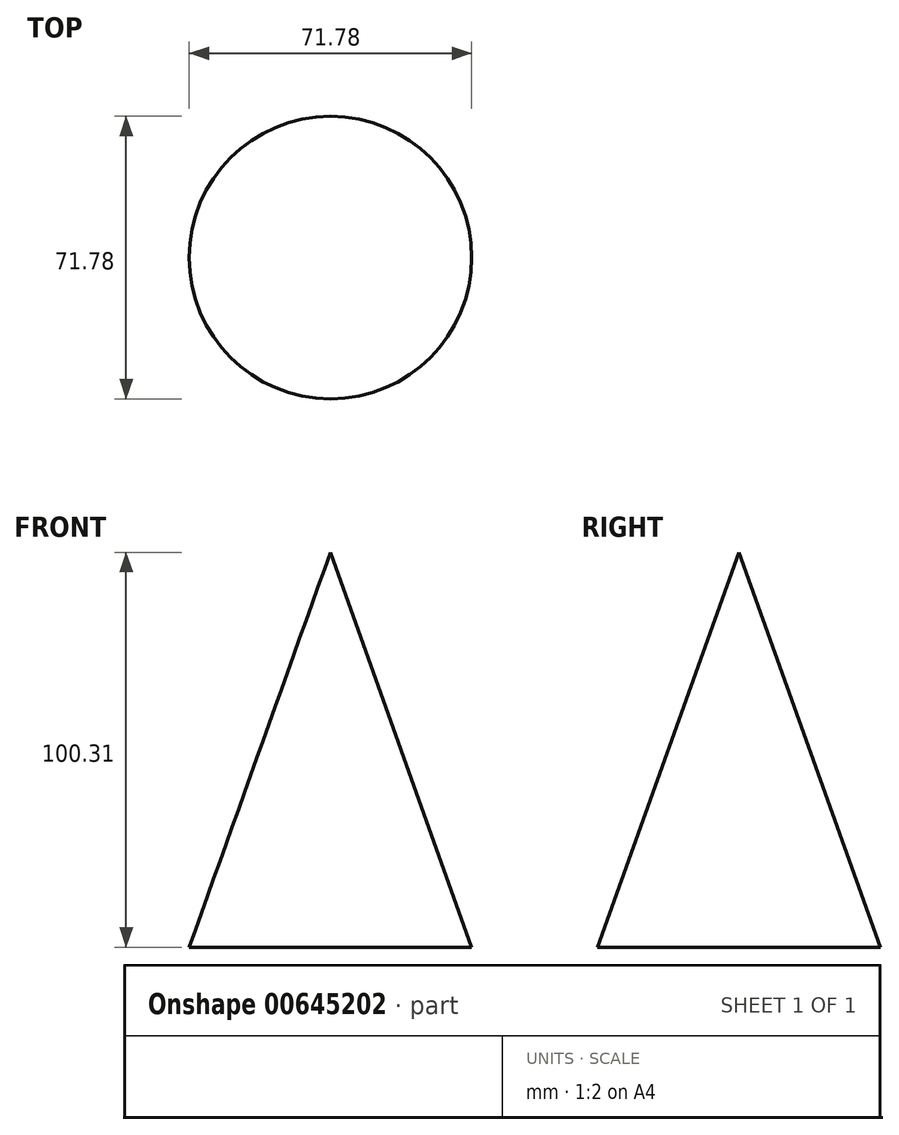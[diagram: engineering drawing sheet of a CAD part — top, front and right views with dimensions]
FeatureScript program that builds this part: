
annotation { "Feature Type Name" : "Feature", "Feature Type Description" : "" }
export const myFeature = defineFeature(function(context is Context, id is Id, definition is map)
    precondition{}
    {
        {
            var Q0;
            Q0=qCreatedBy(makeId("Front.planeOp"),FACE);
            var sketch = newSketch(context, id + "F0", { "sketchPlane" : qUnion([Q0])});
            skLineSegment(sketch, "E0", {"start": v(0, -53.28) * mm, "end": v(0, 47.03) * mm});
            skLineSegment(sketch, "E1", {"start": v(0, 47.03) * mm, "end": v(35.89, -53.28) * mm});
            skLineSegment(sketch, "E2", {"start": v(35.89, -53.28) * mm, "end": v(0, -53.28) * mm});
            skSolve(sketch);
        }
        {
            var Q0;
            Q0=makeQuery(id+"F0.imprint","IMPRINT",FACE,{"disambiguationData":[TD([[makeQuery(id+"F0.imprint","IMPRINT",EDGE,{"derivedFrom":sQuery(id+"F0.wireOp",EDGE,"E0")}),-1.0]])]});
            var Q1;
            Q1=sQuery(id+"F0.wireOp",EDGE,"E0");
            revolve(context, id + "F1", {"entities" : qUnion([Q0]), "axis" : qUnion([Q1]), "revolveType" : RevolveType.FULL});
        }
    });
